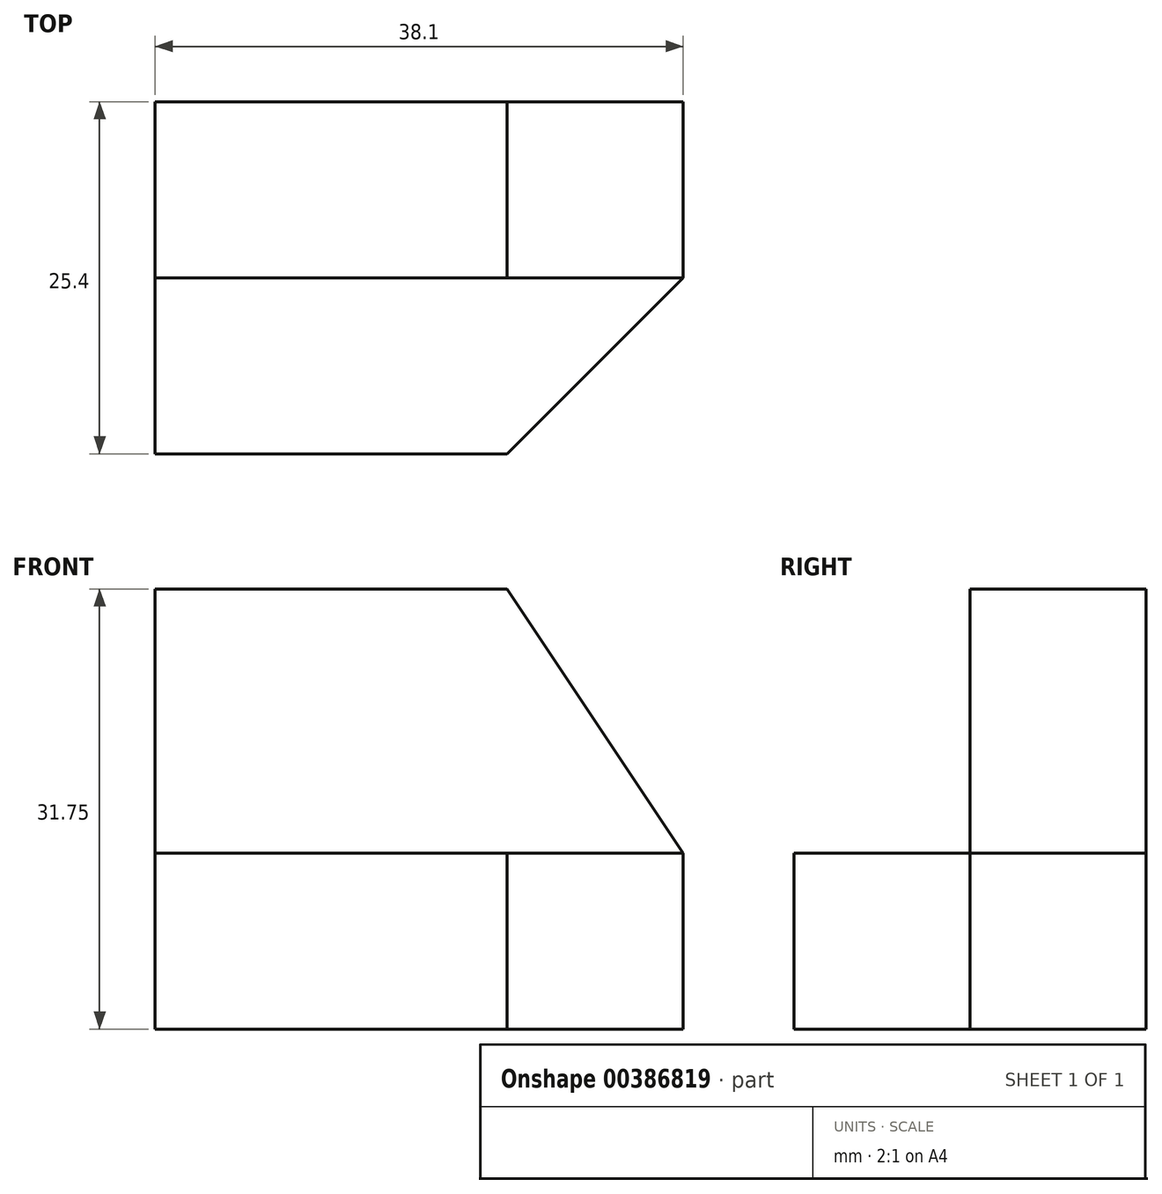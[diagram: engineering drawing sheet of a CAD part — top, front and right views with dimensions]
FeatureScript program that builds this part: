
annotation { "Feature Type Name" : "Feature", "Feature Type Description" : "" }
export const myFeature = defineFeature(function(context is Context, id is Id, definition is map)
    precondition{}
    {
        {
            var Q0;
            Q0=qCreatedBy(makeId("Top.planeOp"),FACE);
            var sketch = newSketch(context, id + "F0", { "sketchPlane" : qUnion([Q0])});
            skLineSegment(sketch, "E0", {"start": v(0, 1.68) * mm, "end": v(0, 27.08) * mm});
            skLineSegment(sketch, "E1", {"start": v(0, 27.08) * mm, "end": v(38.1, 27.08) * mm});
            skLineSegment(sketch, "E2", {"start": v(38.1, 27.08) * mm, "end": v(38.1, 14.38) * mm});
            skLineSegment(sketch, "E3", {"start": v(0, 1.68) * mm, "end": v(25.4, 1.68) * mm});
            skLineSegment(sketch, "E4", {"start": v(25.4, 1.68) * mm, "end": v(38.1, 14.38) * mm});
            skLineSegment(sketch, "E5", {"start": v(38.1, 14.38) * mm, "end": v(0, 14.38) * mm});
            skSolve(sketch);
        }
        {
            var Q0;
            {var subQ0=sQuery(id+"F0.wireOp",EDGE,"E1");Q0=makeQuery(id+"F0.imprint","IMPRINT",FACE,{"disambiguationData":[TD([[makeQuery(id+"F0.imprint","IMPRINT",EDGE,{"derivedFrom":subQ0}),-1.0]])]});}
            var Q1;
            {var subQ0=sQuery(id+"F0.wireOp",EDGE,"E3");Q1=makeQuery(id+"F0.imprint","IMPRINT",FACE,{"disambiguationData":[TD([[makeQuery(id+"F0.imprint","IMPRINT",EDGE,{"derivedFrom":subQ0}),1.0]])]});}
            extrude(context, id + "F1", {"entities" : qUnion([Q0, Q1]), "depth" : 12.7 * mm});
        }
        {
            var Q0;
            Q0=makeQuery(id+"F1.opExtrude","SWEPT_FACE",FACE,{"disambiguationData":[OSD([sQuery(id+"F0.wireOp",EDGE,"E1")])]});
            var sketch = newSketch(context, id + "F2", { "sketchPlane" : qUnion([Q0])});
            skLineSegment(sketch, "E6", {"start": v(0, 0) * mm, "end": v(0, 31.75) * mm});
            skLineSegment(sketch, "E7", {"start": v(0, 31.75) * mm, "end": v(-25.4, 31.75) * mm});
            skLineSegment(sketch, "E8", {"start": v(-25.4, 31.75) * mm, "end": v(-38.1, 12.7) * mm});
            skSolve(sketch);
        }
        {
            var Q0;
            {var subQ2=sQuery(id+"F2.wireOp",EDGE,"E7");Q0=makeQuery(id+"F2.imprint","IMPRINT",FACE,{"disambiguationData":[TD([[makeQuery(id+"F2.imprint","IMPRINT",EDGE,{"derivedFrom":subQ2}),1.0]])]});}
            extrude(context, id + "F3", {"entities" : qUnion([Q0]), "operationType" : NewBodyOperationType.ADD, "oppositeDirection" : true, "depth" : 12.7 * mm});
        }
    });
